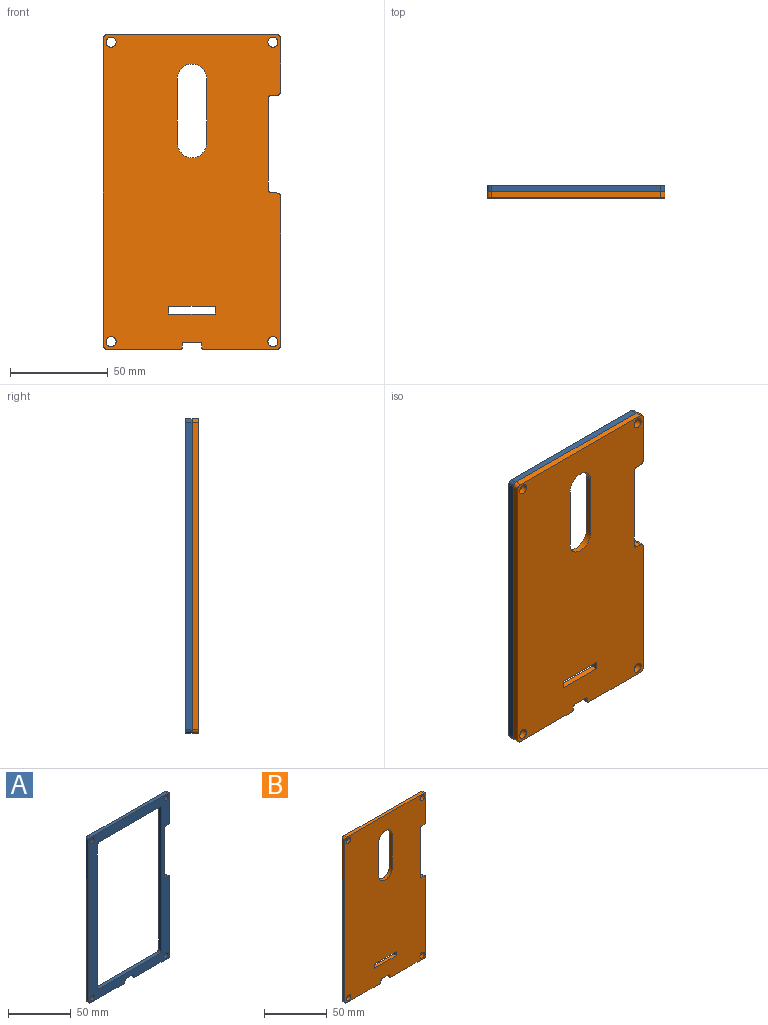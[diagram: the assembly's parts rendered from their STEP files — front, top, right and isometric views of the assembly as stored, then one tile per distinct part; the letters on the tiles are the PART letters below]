
ASSEMBLY  parts=2 mates=1
PART A: 38 faces, bbox 91x3.2x161 mm
  f0: plane 68x3.18mm, normal (0,0,-1), area 215.9mm2, adj f20,f21,f30,f33
  f1: plane 139x3.18mm, normal (-1,0,0), area 441.3mm2, adj f20,f21,f30,f31
  f2: plane 68x3.18mm, normal (0,0,1), area 215.9mm2, adj f20,f21,f31,f32
  f3: plane 46x3.18mm, normal (1,0,0), area 146.1mm2, adj f20,f21,f22,f29
  f4: plane 3.18x2.5mm, normal (0,0,-1), area 7.9mm2, adj f20,f21,f22,f23
  f5: plane 27x3.18mm, normal (1,0,0), area 85.7mm2, adj f20,f21,f23,f24
  f6: plane 87x3.18mm, normal (0,0,1), area 276.2mm2, adj f20,f21,f24,f25
  f7: plane 157x3.18mm, normal (-1,0,0), area 498.5mm2, adj f20,f21,f25,f26
  f8: plane 37.5x3.18mm, normal (0,0,-1), area 119.1mm2, adj f20,f21,f26,f34
  f9: plane 3.18x1.5mm, normal (1,0,0), area 4.8mm2, adj f20,f21,f34,f35
  f10: plane 8x3.18mm, normal (0,0,-1), area 25.4mm2, adj f20,f21,f35,f36
  f11: plane 3.18x1.5mm, normal (-1,0,0), area 4.8mm2, adj f20,f21,f36,f37
  f12: plane 37.5x3.18mm, normal (0,0,-1), area 119.1mm2, adj f20,f21,f27,f37
  f13: plane 76x3.18mm, normal (1,0,0), area 241.3mm2, adj f20,f21,f27,f28
  f14: cylinder r=2.58mm len=5.16mm, axis (0,1,0), area 51.4mm2, adj f20,f21
  f15: cylinder r=2.58mm len=5.16mm, axis (0,1,0), area 51.4mm2, adj f20,f21
  f16: cylinder r=2.58mm len=5.16mm, axis (0,1,0), area 51.4mm2, adj f20,f21
  f17: cylinder r=2.58mm len=5.16mm, axis (0,1,0), area 51.4mm2, adj f20,f21
  f18: plane 3.18x2.5mm, normal (0,0,1), area 7.9mm2, adj f20,f21,f28,f29
  f19: plane 139x3.18mm, normal (1,0,0), area 441.3mm2, adj f20,f21,f32,f33
  f20: plane 161x91mm, normal (0,-1,0), area 3911.5mm2, adj f0,f1,f2,f3,f4,f5,f6,f7
  f21: plane 161x91mm, normal (0,1,0), area 3911.5mm2, adj f0,f1,f2,f3,f4,f5,f6,f7
  f22: cylinder r=2mm len=3.18mm, axis (0,-1,0), area 10mm2, adj f3,f4,f20,f21
  f23: cylinder r=2mm len=3.18mm, axis (0,1,0), area 10mm2, adj f4,f5,f20,f21
  f24: cylinder r=2mm len=3.18mm, axis (0,-1,0), area 10mm2, adj f5,f6,f20,f21
  f25: cylinder r=2mm len=3.18mm, axis (0,1,0), area 10mm2, adj f6,f7,f20,f21
  f26: cylinder r=2mm len=3.18mm, axis (0,-1,0), area 10mm2, adj f7,f8,f20,f21
  f27: cylinder r=2mm len=3.18mm, axis (0,1,0), area 10mm2, adj f12,f13,f20,f21
  f28: cylinder r=2mm len=3.18mm, axis (0,-1,0), area 10mm2, adj f13,f18,f20,f21
  f29: cylinder r=2mm len=3.18mm, axis (0,1,0), area 10mm2, adj f3,f18,f20,f21
  f30: cylinder r=2mm len=3.18mm, axis (0,1,0), area 10mm2, adj f0,f1,f20,f21
  f31: cylinder r=2mm len=3.18mm, axis (0,-1,0), area 10mm2, adj f1,f2,f20,f21
  f32: cylinder r=2mm len=3.18mm, axis (0,1,0), area 10mm2, adj f2,f19,f20,f21
  f33: cylinder r=2mm len=3.18mm, axis (0,-1,0), area 10mm2, adj f0,f19,f20,f21
  f34: cylinder r=1mm len=3.18mm, axis (0,-1,0), area 5mm2, adj f8,f9,f20,f21
  f35: cylinder r=1mm len=3.18mm, axis (0,-1,0), area 5mm2, adj f9,f10,f20,f21
  f36: cylinder r=1mm len=3.18mm, axis (0,1,0), area 5mm2, adj f10,f11,f20,f21
  f37: cylinder r=1mm len=3.18mm, axis (0,1,0), area 5mm2, adj f11,f12,f20,f21
PART B: 38 faces, bbox 91x3.2x161 mm
  f0: plane 24x3.18mm, normal (0,0,-1), area 76.2mm2, adj f1,f23,f24,f25
  f1: plane 4x3.18mm, normal (-1,0,0), area 12.7mm2, adj f0,f2,f24,f25
  f2: plane 24x3.18mm, normal (0,0,1), area 76.2mm2, adj f1,f23,f24,f25
  f3: plane 33x3.18mm, normal (1,0,0), area 104.8mm2, adj f4,f21,f24,f25
  f4: cylinder r=7.5mm len=15mm, axis (0,1,0), area 74.8mm2, adj f3,f5,f24,f25
  f5: plane 33x3.18mm, normal (-1,0,0), area 104.8mm2, adj f4,f21,f24,f25
  f6: plane 46x3.18mm, normal (1,0,0), area 146.1mm2, adj f24,f25,f26,f33
  f7: plane 3.18x2.5mm, normal (0,0,-1), area 7.9mm2, adj f24,f25,f26,f27
  f8: plane 27x3.18mm, normal (1,0,0), area 85.7mm2, adj f24,f25,f27,f28
  f9: plane 87x3.18mm, normal (0,0,1), area 276.2mm2, adj f24,f25,f28,f29
  f10: plane 157x3.18mm, normal (-1,0,0), area 498.5mm2, adj f24,f25,f29,f30
  f11: plane 37.5x3.18mm, normal (0,0,-1), area 119.1mm2, adj f24,f25,f30,f34
  f12: plane 3.18x1.5mm, normal (1,0,0), area 4.8mm2, adj f24,f25,f34,f35
  f13: plane 8x3.18mm, normal (0,0,-1), area 25.4mm2, adj f24,f25,f35,f36
  f14: plane 3.18x1.5mm, normal (-1,0,0), area 4.8mm2, adj f24,f25,f36,f37
  f15: plane 37.5x3.18mm, normal (0,0,-1), area 119.1mm2, adj f24,f25,f31,f37
  f16: plane 76x3.18mm, normal (1,0,0), area 241.3mm2, adj f24,f25,f31,f32
  f17: cylinder r=2.58mm len=5.16mm, axis (0,1,0), area 51.4mm2, adj f24,f25
  f18: cylinder r=2.58mm len=5.16mm, axis (0,1,0), area 51.4mm2, adj f24,f25
  f19: cylinder r=2.58mm len=5.16mm, axis (0,1,0), area 51.4mm2, adj f24,f25
  f20: cylinder r=2.58mm len=5.16mm, axis (0,1,0), area 51.4mm2, adj f24,f25
  f21: cylinder r=7.5mm len=15mm, axis (0,1,0), area 74.8mm2, adj f3,f5,f24,f25
  f22: plane 3.18x2.5mm, normal (0,0,1), area 7.9mm2, adj f24,f25,f32,f33
  f23: plane 4x3.18mm, normal (1,0,0), area 12.7mm2, adj f0,f2,f24,f25
  f24: plane 161x91mm, normal (0,-1,0), area 13436.3mm2, adj f0,f1,f2,f3,f4,f5,f6,f7
  f25: plane 161x91mm, normal (0,1,0), area 13436.3mm2, adj f0,f1,f2,f3,f4,f5,f6,f7
  f26: cylinder r=2mm len=3.18mm, axis (0,-1,0), area 10mm2, adj f6,f7,f24,f25
  f27: cylinder r=2mm len=3.18mm, axis (0,1,0), area 10mm2, adj f7,f8,f24,f25
  f28: cylinder r=2mm len=3.18mm, axis (0,-1,0), area 10mm2, adj f8,f9,f24,f25
  f29: cylinder r=2mm len=3.18mm, axis (0,1,0), area 10mm2, adj f9,f10,f24,f25
  f30: cylinder r=2mm len=3.18mm, axis (0,-1,0), area 10mm2, adj f10,f11,f24,f25
  f31: cylinder r=2mm len=3.18mm, axis (0,1,0), area 10mm2, adj f15,f16,f24,f25
  f32: cylinder r=2mm len=3.18mm, axis (0,-1,0), area 10mm2, adj f16,f22,f24,f25
  f33: cylinder r=2mm len=3.18mm, axis (0,1,0), area 10mm2, adj f6,f22,f24,f25
  f34: cylinder r=1mm len=3.18mm, axis (0,-1,0), area 5mm2, adj f11,f12,f24,f25
  f35: cylinder r=1mm len=3.18mm, axis (0,-1,0), area 5mm2, adj f12,f13,f24,f25
  f36: cylinder r=1mm len=3.18mm, axis (0,1,0), area 5mm2, adj f13,f14,f24,f25
  f37: cylinder r=1mm len=3.18mm, axis (0,1,0), area 5mm2, adj f14,f15,f24,f25
PLACE A t=(-98.13,-53.89,17.92)mm
PLACE B t=(-98.13,-57.07,17.92)mm
MATE planar A.f20 <-> B.f25  axis (0,-1,0) through (-98.13,-57.07,98.42)mm
